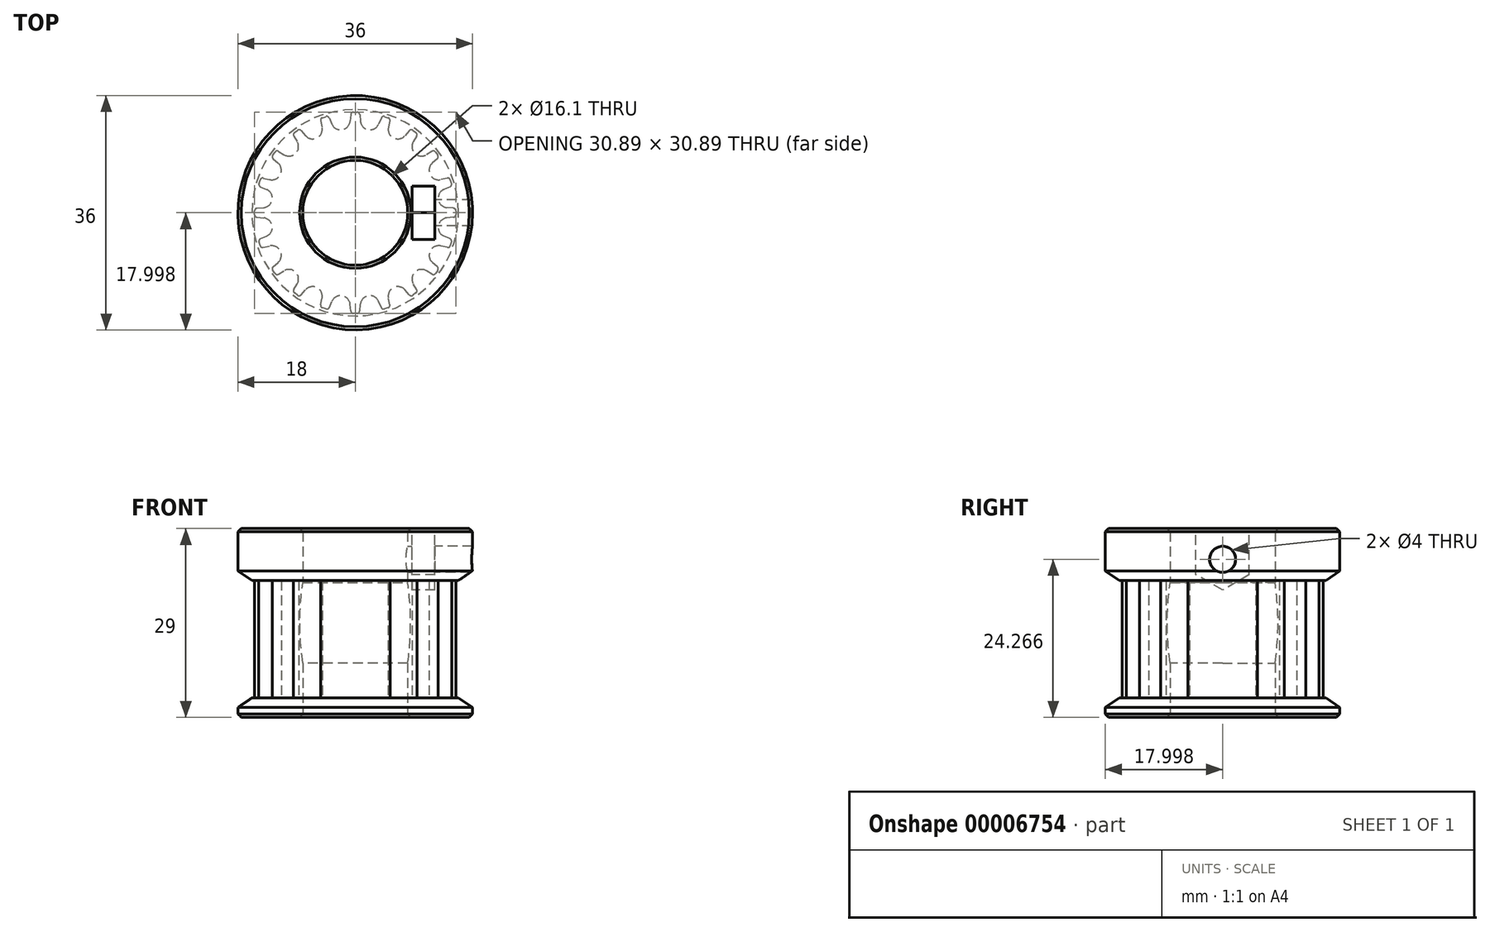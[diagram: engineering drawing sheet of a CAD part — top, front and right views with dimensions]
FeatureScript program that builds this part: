
annotation { "Feature Type Name" : "Feature", "Feature Type Description" : "" }
export const myFeature = defineFeature(function(context is Context, id is Id, definition is map)
    precondition{}
    {
        {
            var Q0;
            Q0=qCreatedBy(makeId("Top.planeOp"),FACE);
            var sketch = newSketch(context, id + "F0", { "sketchPlane" : qUnion([Q0])});
            skLineSegment(sketch, "E0", {"start": v(-0.3, 10.1) * mm, "end": v(0.3, 10.1) * mm});
            skPoint(sketch, "E1", {"position": v(0, 10.1) * mm});
            skArc(sketch, "E2", {"start": v(0.3, 10.1) * mm, "mid": v(0.57, 9.99) * mm, "end": v(0.7, 9.73) * mm});
            skArc(sketch, "E3", {"start": v(-0.3, 10.1) * mm, "mid": v(-0.57, 9.99) * mm, "end": v(-0.7, 9.73) * mm});
            skLineSegment(sketch, "E4", {"start": v(-0.7, 9.73) * mm, "end": v(-0.79, 8.73) * mm});
            skLineSegment(sketch, "E5", {"start": v(0.7, 9.73) * mm, "end": v(0.79, 8.73) * mm});
            skArc(sketch, "E6", {"start": v(-0.79, 8.73) * mm, "mid": v(-2.02, 7.4) * mm, "end": v(-3.6, 8.29) * mm});
            skArc(sketch, "E7.1.0", {"start": v(-5.1, 7.8) * mm, "mid": v(-5.87, 6.16) * mm, "end": v(-7.64, 6.5) * mm});
            skLineSegment(sketch, "E7.1.1", {"start": v(-5.32, 8.77) * mm, "end": v(-5.1, 7.8) * mm});
            skArc(sketch, "E7.1.2", {"start": v(-5.06, 9.25) * mm, "mid": v(-5.28, 9.06) * mm, "end": v(-5.32, 8.77) * mm});
            skLineSegment(sketch, "E7.1.3", {"start": v(-5.06, 9.25) * mm, "end": v(-4.49, 9.43) * mm});
            skArc(sketch, "E7.1.4", {"start": v(-4.49, 9.43) * mm, "mid": v(-4.2, 9.41) * mm, "end": v(-4, 9.2) * mm});
            skLineSegment(sketch, "E7.1.5", {"start": v(-4, 9.2) * mm, "end": v(-3.6, 8.29) * mm});
            skArc(sketch, "E7.2.0", {"start": v(-8.91, 5.58) * mm, "mid": v(-9.14, 3.78) * mm, "end": v(-10.93, 3.56) * mm});
            skLineSegment(sketch, "E7.2.1", {"start": v(-9.43, 6.44) * mm, "end": v(-8.91, 5.58) * mm});
            skArc(sketch, "E7.2.2", {"start": v(-9.32, 6.97) * mm, "mid": v(-9.48, 6.72) * mm, "end": v(-9.43, 6.44) * mm});
            skLineSegment(sketch, "E7.2.3", {"start": v(-9.32, 6.97) * mm, "end": v(-8.84, 7.32) * mm});
            skArc(sketch, "E7.2.4", {"start": v(-8.84, 7.32) * mm, "mid": v(-8.56, 7.4) * mm, "end": v(-8.3, 7.26) * mm});
            skLineSegment(sketch, "E7.2.5", {"start": v(-8.3, 7.26) * mm, "end": v(-7.64, 6.5) * mm});
            skPoint(sketch, "E7.center", {"position": v(0, -5.35) * mm});
            skArc(sketch, "E8.3.3.0", {"start": v(-11.86, 2.3) * mm, "mid": v(-11.51, 0.51) * mm, "end": v(-13.15, -0.25) * mm});
            skLineSegment(sketch, "E8.4.3.0", {"start": v(-12.61, 2.95) * mm, "end": v(-11.86, 2.3) * mm});
            skArc(sketch, "E8.7.3.0", {"start": v(-12.67, 3.48) * mm, "mid": v(-12.75, 3.2) * mm, "end": v(-12.61, 2.95) * mm});
            skLineSegment(sketch, "E8.11.3.0", {"start": v(-12.67, 3.48) * mm, "end": v(-12.32, 3.97) * mm});
            skArc(sketch, "E8.14.3.0", {"start": v(-12.32, 3.97) * mm, "mid": v(-12.08, 4.13) * mm, "end": v(-11.8, 4.08) * mm});
            skLineSegment(sketch, "E8.18.3.0", {"start": v(-11.8, 4.08) * mm, "end": v(-10.93, 3.56) * mm});
            skArc(sketch, "E8.3.4.0", {"start": v(-13.64, -1.75) * mm, "mid": v(-12.76, -3.33) * mm, "end": v(-14.08, -4.57) * mm});
            skLineSegment(sketch, "E8.4.4.0", {"start": v(-14.56, -1.36) * mm, "end": v(-13.64, -1.75) * mm});
            skArc(sketch, "E8.7.4.0", {"start": v(-14.78, -0.86) * mm, "mid": v(-14.77, -1.15) * mm, "end": v(-14.56, -1.36) * mm});
            skLineSegment(sketch, "E8.11.4.0", {"start": v(-14.78, -0.86) * mm, "end": v(-14.6, -0.3) * mm});
            skArc(sketch, "E8.14.4.0", {"start": v(-14.6, -0.3) * mm, "mid": v(-14.41, -0.07) * mm, "end": v(-14.13, -0.03) * mm});
            skLineSegment(sketch, "E8.18.4.0", {"start": v(-14.13, -0.03) * mm, "end": v(-13.15, -0.25) * mm});
            skArc(sketch, "E8.3.5.0", {"start": v(-14.08, -6.14) * mm, "mid": v(-12.76, -7.37) * mm, "end": v(-13.64, -8.96) * mm});
            skLineSegment(sketch, "E8.4.5.0", {"start": v(-15.08, -6.05) * mm, "end": v(-14.08, -6.14) * mm});
            skArc(sketch, "E8.7.5.0", {"start": v(-15.45, -5.65) * mm, "mid": v(-15.34, -5.92) * mm, "end": v(-15.08, -6.05) * mm});
            skLineSegment(sketch, "E8.11.5.0", {"start": v(-15.45, -5.65) * mm, "end": v(-15.45, -5.05) * mm});
            skArc(sketch, "E8.14.5.0", {"start": v(-15.45, -5.05) * mm, "mid": v(-15.34, -4.78) * mm, "end": v(-15.08, -4.65) * mm});
            skLineSegment(sketch, "E8.18.5.0", {"start": v(-15.08, -4.65) * mm, "end": v(-14.08, -4.57) * mm});
            skArc(sketch, "E8.3.6.0", {"start": v(-13.15, -10.45) * mm, "mid": v(-11.51, -11.22) * mm, "end": v(-11.86, -13) * mm});
            skLineSegment(sketch, "E8.4.6.0", {"start": v(-14.13, -10.68) * mm, "end": v(-13.15, -10.45) * mm});
            skArc(sketch, "E8.7.6.0", {"start": v(-14.6, -10.41) * mm, "mid": v(-14.41, -10.63) * mm, "end": v(-14.13, -10.68) * mm});
            skLineSegment(sketch, "E8.11.6.0", {"start": v(-14.6, -10.41) * mm, "end": v(-14.78, -9.84) * mm});
            skArc(sketch, "E8.14.6.0", {"start": v(-14.78, -9.84) * mm, "mid": v(-14.77, -9.55) * mm, "end": v(-14.56, -9.35) * mm});
            skLineSegment(sketch, "E8.18.6.0", {"start": v(-14.56, -9.35) * mm, "end": v(-13.64, -8.96) * mm});
            skArc(sketch, "E8.3.7.0", {"start": v(-10.93, -14.27) * mm, "mid": v(-9.14, -14.49) * mm, "end": v(-8.91, -16.28) * mm});
            skLineSegment(sketch, "E8.4.7.0", {"start": v(-11.8, -14.78) * mm, "end": v(-10.93, -14.27) * mm});
            skArc(sketch, "E8.7.7.0", {"start": v(-12.32, -14.67) * mm, "mid": v(-12.08, -14.83) * mm, "end": v(-11.8, -14.78) * mm});
            skLineSegment(sketch, "E8.11.7.0", {"start": v(-12.32, -14.67) * mm, "end": v(-12.67, -14.19) * mm});
            skArc(sketch, "E8.14.7.0", {"start": v(-12.67, -14.19) * mm, "mid": v(-12.75, -13.9) * mm, "end": v(-12.61, -13.65) * mm});
            skLineSegment(sketch, "E8.18.7.0", {"start": v(-12.61, -13.65) * mm, "end": v(-11.86, -13) * mm});
            skArc(sketch, "E8.3.8.0", {"start": v(-7.64, -17.2) * mm, "mid": v(-5.87, -16.86) * mm, "end": v(-5.1, -18.5) * mm});
            skLineSegment(sketch, "E8.4.8.0", {"start": v(-8.3, -17.96) * mm, "end": v(-7.64, -17.2) * mm});
            skArc(sketch, "E8.7.8.0", {"start": v(-8.84, -18.02) * mm, "mid": v(-8.56, -18.1) * mm, "end": v(-8.3, -17.96) * mm});
            skLineSegment(sketch, "E8.11.8.0", {"start": v(-8.84, -18.02) * mm, "end": v(-9.32, -17.67) * mm});
            skArc(sketch, "E8.14.8.0", {"start": v(-9.32, -17.67) * mm, "mid": v(-9.48, -17.43) * mm, "end": v(-9.43, -17.14) * mm});
            skLineSegment(sketch, "E8.18.8.0", {"start": v(-9.43, -17.14) * mm, "end": v(-8.91, -16.28) * mm});
            skArc(sketch, "E8.3.9.0", {"start": v(-3.6, -18.99) * mm, "mid": v(-2.02, -18.11) * mm, "end": v(-0.79, -19.44) * mm});
            skLineSegment(sketch, "E8.4.9.0", {"start": v(-4, -19.91) * mm, "end": v(-3.6, -18.99) * mm});
            skArc(sketch, "E8.7.9.0", {"start": v(-4.49, -20.13) * mm, "mid": v(-4.2, -20.12) * mm, "end": v(-4, -19.91) * mm});
            skLineSegment(sketch, "E8.11.9.0", {"start": v(-4.49, -20.13) * mm, "end": v(-5.06, -19.95) * mm});
            skArc(sketch, "E8.14.9.0", {"start": v(-5.06, -19.95) * mm, "mid": v(-5.28, -19.77) * mm, "end": v(-5.32, -19.48) * mm});
            skLineSegment(sketch, "E8.18.9.0", {"start": v(-5.32, -19.48) * mm, "end": v(-5.1, -18.5) * mm});
            skArc(sketch, "E8.3.10.0", {"start": v(0.79, -19.44) * mm, "mid": v(2.02, -18.11) * mm, "end": v(3.6, -18.99) * mm});
            skLineSegment(sketch, "E8.4.10.0", {"start": v(0.7, -20.43) * mm, "end": v(0.79, -19.44) * mm});
            skArc(sketch, "E8.7.10.0", {"start": v(0.3, -20.8) * mm, "mid": v(0.57, -20.7) * mm, "end": v(0.7, -20.43) * mm});
            skLineSegment(sketch, "E8.11.10.0", {"start": v(0.3, -20.8) * mm, "end": v(-0.3, -20.8) * mm});
            skArc(sketch, "E8.14.10.0", {"start": v(-0.3, -20.8) * mm, "mid": v(-0.57, -20.7) * mm, "end": v(-0.7, -20.43) * mm});
            skLineSegment(sketch, "E8.18.10.0", {"start": v(-0.7, -20.43) * mm, "end": v(-0.79, -19.44) * mm});
            skArc(sketch, "E8.3.11.0", {"start": v(5.1, -18.5) * mm, "mid": v(5.87, -16.86) * mm, "end": v(7.64, -17.2) * mm});
            skLineSegment(sketch, "E8.4.11.0", {"start": v(5.32, -19.48) * mm, "end": v(5.1, -18.5) * mm});
            skArc(sketch, "E8.7.11.0", {"start": v(5.06, -19.95) * mm, "mid": v(5.28, -19.77) * mm, "end": v(5.32, -19.48) * mm});
            skLineSegment(sketch, "E8.11.11.0", {"start": v(5.06, -19.95) * mm, "end": v(4.49, -20.13) * mm});
            skArc(sketch, "E8.14.11.0", {"start": v(4.49, -20.13) * mm, "mid": v(4.2, -20.12) * mm, "end": v(4, -19.91) * mm});
            skLineSegment(sketch, "E8.18.11.0", {"start": v(4, -19.91) * mm, "end": v(3.6, -18.99) * mm});
            skArc(sketch, "E8.3.12.0", {"start": v(8.91, -16.28) * mm, "mid": v(9.14, -14.49) * mm, "end": v(10.93, -14.27) * mm});
            skLineSegment(sketch, "E8.4.12.0", {"start": v(9.43, -17.14) * mm, "end": v(8.91, -16.28) * mm});
            skArc(sketch, "E8.7.12.0", {"start": v(9.32, -17.67) * mm, "mid": v(9.48, -17.43) * mm, "end": v(9.43, -17.14) * mm});
            skLineSegment(sketch, "E8.11.12.0", {"start": v(9.32, -17.67) * mm, "end": v(8.84, -18.02) * mm});
            skArc(sketch, "E8.14.12.0", {"start": v(8.84, -18.02) * mm, "mid": v(8.56, -18.1) * mm, "end": v(8.3, -17.96) * mm});
            skLineSegment(sketch, "E8.18.12.0", {"start": v(8.3, -17.96) * mm, "end": v(7.64, -17.2) * mm});
            skArc(sketch, "E8.3.13.0", {"start": v(11.86, -13) * mm, "mid": v(11.51, -11.22) * mm, "end": v(13.15, -10.45) * mm});
            skLineSegment(sketch, "E8.4.13.0", {"start": v(12.61, -13.65) * mm, "end": v(11.86, -13) * mm});
            skArc(sketch, "E8.7.13.0", {"start": v(12.67, -14.19) * mm, "mid": v(12.75, -13.9) * mm, "end": v(12.61, -13.65) * mm});
            skLineSegment(sketch, "E8.11.13.0", {"start": v(12.67, -14.19) * mm, "end": v(12.32, -14.67) * mm});
            skArc(sketch, "E8.14.13.0", {"start": v(12.32, -14.67) * mm, "mid": v(12.08, -14.83) * mm, "end": v(11.8, -14.78) * mm});
            skLineSegment(sketch, "E8.18.13.0", {"start": v(11.8, -14.78) * mm, "end": v(10.93, -14.27) * mm});
            skCircle(sketch, "E9", {"center": v(0, -5.35) * mm, "radius": 15.45 * mm, "construction": true});
            skArc(sketch, "E10.3.14.0", {"start": v(13.64, -8.96) * mm, "mid": v(12.76, -7.37) * mm, "end": v(14.08, -6.14) * mm});
            skLineSegment(sketch, "E10.4.14.0", {"start": v(14.56, -9.35) * mm, "end": v(13.64, -8.96) * mm});
            skArc(sketch, "E10.7.14.0", {"start": v(14.78, -9.84) * mm, "mid": v(14.77, -9.55) * mm, "end": v(14.56, -9.35) * mm});
            skLineSegment(sketch, "E10.11.14.0", {"start": v(14.78, -9.84) * mm, "end": v(14.6, -10.41) * mm});
            skArc(sketch, "E10.14.14.0", {"start": v(14.6, -10.41) * mm, "mid": v(14.41, -10.63) * mm, "end": v(14.13, -10.68) * mm});
            skLineSegment(sketch, "E10.18.14.0", {"start": v(14.13, -10.68) * mm, "end": v(13.15, -10.45) * mm});
            skArc(sketch, "E10.3.15.0", {"start": v(14.08, -4.57) * mm, "mid": v(12.76, -3.33) * mm, "end": v(13.64, -1.75) * mm});
            skLineSegment(sketch, "E10.4.15.0", {"start": v(15.08, -4.65) * mm, "end": v(14.08, -4.57) * mm});
            skArc(sketch, "E10.7.15.0", {"start": v(15.45, -5.05) * mm, "mid": v(15.34, -4.78) * mm, "end": v(15.08, -4.65) * mm});
            skLineSegment(sketch, "E10.11.15.0", {"start": v(15.45, -5.05) * mm, "end": v(15.45, -5.65) * mm});
            skArc(sketch, "E10.14.15.0", {"start": v(15.45, -5.65) * mm, "mid": v(15.34, -5.92) * mm, "end": v(15.08, -6.05) * mm});
            skLineSegment(sketch, "E10.18.15.0", {"start": v(15.08, -6.05) * mm, "end": v(14.08, -6.14) * mm});
            skArc(sketch, "E10.3.16.0", {"start": v(13.15, -0.25) * mm, "mid": v(11.51, 0.51) * mm, "end": v(11.86, 2.3) * mm});
            skLineSegment(sketch, "E10.4.16.0", {"start": v(14.13, -0.03) * mm, "end": v(13.15, -0.25) * mm});
            skArc(sketch, "E10.7.16.0", {"start": v(14.6, -0.3) * mm, "mid": v(14.41, -0.07) * mm, "end": v(14.13, -0.03) * mm});
            skLineSegment(sketch, "E10.11.16.0", {"start": v(14.6, -0.3) * mm, "end": v(14.78, -0.86) * mm});
            skArc(sketch, "E10.14.16.0", {"start": v(14.78, -0.86) * mm, "mid": v(14.77, -1.15) * mm, "end": v(14.56, -1.36) * mm});
            skLineSegment(sketch, "E10.18.16.0", {"start": v(14.56, -1.36) * mm, "end": v(13.64, -1.75) * mm});
            skArc(sketch, "E10.3.17.0", {"start": v(10.93, 3.56) * mm, "mid": v(9.14, 3.78) * mm, "end": v(8.91, 5.58) * mm});
            skLineSegment(sketch, "E10.4.17.0", {"start": v(11.8, 4.08) * mm, "end": v(10.93, 3.56) * mm});
            skArc(sketch, "E10.7.17.0", {"start": v(12.32, 3.97) * mm, "mid": v(12.08, 4.13) * mm, "end": v(11.8, 4.08) * mm});
            skLineSegment(sketch, "E10.11.17.0", {"start": v(12.32, 3.97) * mm, "end": v(12.67, 3.48) * mm});
            skArc(sketch, "E10.14.17.0", {"start": v(12.67, 3.48) * mm, "mid": v(12.75, 3.2) * mm, "end": v(12.61, 2.95) * mm});
            skLineSegment(sketch, "E10.18.17.0", {"start": v(12.61, 2.95) * mm, "end": v(11.86, 2.3) * mm});
            skArc(sketch, "E10.3.18.0", {"start": v(7.64, 6.5) * mm, "mid": v(5.87, 6.16) * mm, "end": v(5.1, 7.8) * mm});
            skLineSegment(sketch, "E10.4.18.0", {"start": v(8.3, 7.26) * mm, "end": v(7.64, 6.5) * mm});
            skArc(sketch, "E10.7.18.0", {"start": v(8.84, 7.32) * mm, "mid": v(8.56, 7.4) * mm, "end": v(8.3, 7.26) * mm});
            skLineSegment(sketch, "E10.11.18.0", {"start": v(8.84, 7.32) * mm, "end": v(9.32, 6.97) * mm});
            skArc(sketch, "E10.14.18.0", {"start": v(9.32, 6.97) * mm, "mid": v(9.48, 6.72) * mm, "end": v(9.43, 6.44) * mm});
            skLineSegment(sketch, "E10.18.18.0", {"start": v(9.43, 6.44) * mm, "end": v(8.91, 5.58) * mm});
            skArc(sketch, "E10.3.19.0", {"start": v(3.6, 8.29) * mm, "mid": v(2.02, 7.4) * mm, "end": v(0.79, 8.73) * mm});
            skLineSegment(sketch, "E10.4.19.0", {"start": v(4, 9.2) * mm, "end": v(3.6, 8.29) * mm});
            skArc(sketch, "E10.7.19.0", {"start": v(4.49, 9.43) * mm, "mid": v(4.2, 9.41) * mm, "end": v(4, 9.2) * mm});
            skLineSegment(sketch, "E10.11.19.0", {"start": v(4.49, 9.43) * mm, "end": v(5.06, 9.25) * mm});
            skArc(sketch, "E10.14.19.0", {"start": v(5.06, 9.25) * mm, "mid": v(5.28, 9.06) * mm, "end": v(5.32, 8.77) * mm});
            skLineSegment(sketch, "E10.18.19.0", {"start": v(5.32, 8.77) * mm, "end": v(5.1, 7.8) * mm});
            skCircle(sketch, "E11", {"center": v(0, -5.35) * mm, "radius": 8.05 * mm});
            skSolve(sketch);
        }
        {
            var Q0;
            Q0=makeQuery(id+"F0.imprint","IMPRINT",FACE,{"disambiguationData":[TD([[makeQuery(id+"F0.imprint","IMPRINT",EDGE,{"derivedFrom":sQuery(id+"F0.wireOp",EDGE,"E0")}),-1.0]])]});
            extrude(context, id + "F1", {"entities" : qUnion([Q0]), "endBound" : BoundingType.SYMMETRIC, "depth" : 18 * mm, "offsetDistance" : 25 * mm});
        }
        {
            var Q0;
            Q0=makeQuery(id+"F1.opExtrude","CAP_FACE",FACE,{"disambiguationData":[OSD([sQuery(id+"F0.wireOp",EDGE,"E0"),sQuery(id+"F0.wireOp",EDGE,"E2"),sQuery(id+"F0.wireOp",EDGE,"E3"),sQuery(id+"F0.wireOp",EDGE,"E4"),sQuery(id+"F0.wireOp",EDGE,"E5"),sQuery(id+"F0.wireOp",EDGE,"E6"),sQuery(id+"F0.wireOp",EDGE,"E7.1.0"),sQuery(id+"F0.wireOp",EDGE,"E7.1.1"),sQuery(id+"F0.wireOp",EDGE,"E7.1.2"),sQuery(id+"F0.wireOp",EDGE,"E7.1.3"),sQuery(id+"F0.wireOp",EDGE,"E7.1.4"),sQuery(id+"F0.wireOp",EDGE,"E7.1.5"),sQuery(id+"F0.wireOp",EDGE,"E7.2.0"),sQuery(id+"F0.wireOp",EDGE,"E7.2.1"),sQuery(id+"F0.wireOp",EDGE,"E7.2.2"),sQuery(id+"F0.wireOp",EDGE,"E7.2.3"),sQuery(id+"F0.wireOp",EDGE,"E7.2.4"),sQuery(id+"F0.wireOp",EDGE,"E7.2.5"),sQuery(id+"F0.wireOp",EDGE,"E8.3.3.0"),sQuery(id+"F0.wireOp",EDGE,"E8.4.3.0"),sQuery(id+"F0.wireOp",EDGE,"E8.7.3.0"),sQuery(id+"F0.wireOp",EDGE,"E8.11.3.0"),sQuery(id+"F0.wireOp",EDGE,"E8.14.3.0"),sQuery(id+"F0.wireOp",EDGE,"E8.18.3.0"),sQuery(id+"F0.wireOp",EDGE,"E8.3.4.0"),sQuery(id+"F0.wireOp",EDGE,"E8.4.4.0"),sQuery(id+"F0.wireOp",EDGE,"E8.7.4.0"),sQuery(id+"F0.wireOp",EDGE,"E8.11.4.0"),sQuery(id+"F0.wireOp",EDGE,"E8.14.4.0"),sQuery(id+"F0.wireOp",EDGE,"E8.18.4.0"),sQuery(id+"F0.wireOp",EDGE,"E8.3.5.0"),sQuery(id+"F0.wireOp",EDGE,"E8.4.5.0"),sQuery(id+"F0.wireOp",EDGE,"E8.7.5.0"),sQuery(id+"F0.wireOp",EDGE,"E8.11.5.0"),sQuery(id+"F0.wireOp",EDGE,"E8.14.5.0"),sQuery(id+"F0.wireOp",EDGE,"E8.18.5.0"),sQuery(id+"F0.wireOp",EDGE,"E8.3.6.0"),sQuery(id+"F0.wireOp",EDGE,"E8.4.6.0"),sQuery(id+"F0.wireOp",EDGE,"E8.7.6.0"),sQuery(id+"F0.wireOp",EDGE,"E8.11.6.0"),sQuery(id+"F0.wireOp",EDGE,"E8.14.6.0"),sQuery(id+"F0.wireOp",EDGE,"E8.18.6.0"),sQuery(id+"F0.wireOp",EDGE,"E8.3.7.0"),sQuery(id+"F0.wireOp",EDGE,"E8.4.7.0"),sQuery(id+"F0.wireOp",EDGE,"E8.7.7.0"),sQuery(id+"F0.wireOp",EDGE,"E8.11.7.0"),sQuery(id+"F0.wireOp",EDGE,"E8.14.7.0"),sQuery(id+"F0.wireOp",EDGE,"E8.18.7.0"),sQuery(id+"F0.wireOp",EDGE,"E8.3.8.0"),sQuery(id+"F0.wireOp",EDGE,"E8.4.8.0"),sQuery(id+"F0.wireOp",EDGE,"E8.7.8.0"),sQuery(id+"F0.wireOp",EDGE,"E8.11.8.0"),sQuery(id+"F0.wireOp",EDGE,"E8.14.8.0"),sQuery(id+"F0.wireOp",EDGE,"E8.18.8.0"),sQuery(id+"F0.wireOp",EDGE,"E8.3.9.0"),sQuery(id+"F0.wireOp",EDGE,"E8.4.9.0"),sQuery(id+"F0.wireOp",EDGE,"E8.7.9.0"),sQuery(id+"F0.wireOp",EDGE,"E8.11.9.0"),sQuery(id+"F0.wireOp",EDGE,"E8.14.9.0"),sQuery(id+"F0.wireOp",EDGE,"E8.18.9.0"),sQuery(id+"F0.wireOp",EDGE,"E8.3.10.0"),sQuery(id+"F0.wireOp",EDGE,"E8.4.10.0"),sQuery(id+"F0.wireOp",EDGE,"E8.7.10.0"),sQuery(id+"F0.wireOp",EDGE,"E8.11.10.0"),sQuery(id+"F0.wireOp",EDGE,"E8.14.10.0"),sQuery(id+"F0.wireOp",EDGE,"E8.18.10.0"),sQuery(id+"F0.wireOp",EDGE,"E8.3.11.0"),sQuery(id+"F0.wireOp",EDGE,"E8.4.11.0"),sQuery(id+"F0.wireOp",EDGE,"E8.7.11.0"),sQuery(id+"F0.wireOp",EDGE,"E8.11.11.0"),sQuery(id+"F0.wireOp",EDGE,"E8.14.11.0"),sQuery(id+"F0.wireOp",EDGE,"E8.18.11.0"),sQuery(id+"F0.wireOp",EDGE,"E8.3.12.0"),sQuery(id+"F0.wireOp",EDGE,"E8.4.12.0"),sQuery(id+"F0.wireOp",EDGE,"E8.7.12.0"),sQuery(id+"F0.wireOp",EDGE,"E8.11.12.0"),sQuery(id+"F0.wireOp",EDGE,"E8.14.12.0"),sQuery(id+"F0.wireOp",EDGE,"E8.18.12.0"),sQuery(id+"F0.wireOp",EDGE,"E8.3.13.0"),sQuery(id+"F0.wireOp",EDGE,"E8.4.13.0"),sQuery(id+"F0.wireOp",EDGE,"E8.7.13.0"),sQuery(id+"F0.wireOp",EDGE,"E8.11.13.0"),sQuery(id+"F0.wireOp",EDGE,"E8.14.13.0"),sQuery(id+"F0.wireOp",EDGE,"E8.18.13.0"),sQuery(id+"F0.wireOp",EDGE,"E10.3.14.0"),sQuery(id+"F0.wireOp",EDGE,"E10.4.14.0"),sQuery(id+"F0.wireOp",EDGE,"E10.7.14.0"),sQuery(id+"F0.wireOp",EDGE,"E10.11.14.0"),sQuery(id+"F0.wireOp",EDGE,"E10.14.14.0"),sQuery(id+"F0.wireOp",EDGE,"E10.18.14.0"),sQuery(id+"F0.wireOp",EDGE,"E10.3.15.0"),sQuery(id+"F0.wireOp",EDGE,"E10.4.15.0"),sQuery(id+"F0.wireOp",EDGE,"E10.7.15.0"),sQuery(id+"F0.wireOp",EDGE,"E10.11.15.0"),sQuery(id+"F0.wireOp",EDGE,"E10.14.15.0"),sQuery(id+"F0.wireOp",EDGE,"E10.18.15.0"),sQuery(id+"F0.wireOp",EDGE,"E10.3.16.0"),sQuery(id+"F0.wireOp",EDGE,"E10.4.16.0"),sQuery(id+"F0.wireOp",EDGE,"E10.7.16.0"),sQuery(id+"F0.wireOp",EDGE,"E10.11.16.0"),sQuery(id+"F0.wireOp",EDGE,"E10.14.16.0"),sQuery(id+"F0.wireOp",EDGE,"E10.18.16.0"),sQuery(id+"F0.wireOp",EDGE,"E10.3.17.0"),sQuery(id+"F0.wireOp",EDGE,"E10.4.17.0"),sQuery(id+"F0.wireOp",EDGE,"E10.7.17.0"),sQuery(id+"F0.wireOp",EDGE,"E10.11.17.0"),sQuery(id+"F0.wireOp",EDGE,"E10.14.17.0"),sQuery(id+"F0.wireOp",EDGE,"E10.18.17.0"),sQuery(id+"F0.wireOp",EDGE,"E10.3.18.0"),sQuery(id+"F0.wireOp",EDGE,"E10.4.18.0"),sQuery(id+"F0.wireOp",EDGE,"E10.7.18.0"),sQuery(id+"F0.wireOp",EDGE,"E10.11.18.0"),sQuery(id+"F0.wireOp",EDGE,"E10.14.18.0"),sQuery(id+"F0.wireOp",EDGE,"E10.18.18.0"),sQuery(id+"F0.wireOp",EDGE,"E10.3.19.0"),sQuery(id+"F0.wireOp",EDGE,"E10.4.19.0"),sQuery(id+"F0.wireOp",EDGE,"E10.7.19.0"),sQuery(id+"F0.wireOp",EDGE,"E10.11.19.0"),sQuery(id+"F0.wireOp",EDGE,"E10.14.19.0"),sQuery(id+"F0.wireOp",EDGE,"E10.18.19.0")])],"isStart":false});
            var sketch = newSketch(context, id + "F2", { "sketchPlane" : qUnion([Q0])});
            skCircle(sketch, "E12", {"center": v(0, -5.35) * mm, "radius": 18 * mm});
            skSolve(sketch);
        }
        {
            var Q0;
            Q0=makeQuery(id+"F2.imprint","IMPRINT",FACE,{"disambiguationData":[TD([[makeQuery(id+"F2.imprint","IMPRINT",EDGE,{"derivedFrom":makeQuery(id+"F1.opExtrude","CAP_EDGE",EDGE,{"disambiguationData":[OSD([sQuery(id+"F0.wireOp",EDGE,"E0")])],"isStart":false})}),-1.0]])]});
            var Q1;
            Q1=makeQuery(id+"F2.imprint","IMPRINT",FACE,{"disambiguationData":[TD([[makeQuery(id+"F2.imprint","IMPRINT",EDGE,{"derivedFrom":sQuery(id+"F2.wireOp",EDGE,"E12")}),1.0]])]});
            extrude(context, id + "F3", {"entities" : qUnion([Q0, Q1]), "operationType" : NewBodyOperationType.ADD, "depth" : 8 * mm, "offsetDistance" : 25 * mm});
        }
        {
            var Q0;
            Q0=makeQuery(id+"F1.opExtrude","CAP_FACE",FACE,{"disambiguationData":[OSD([sQuery(id+"F0.wireOp",EDGE,"E0"),sQuery(id+"F0.wireOp",EDGE,"E2"),sQuery(id+"F0.wireOp",EDGE,"E3"),sQuery(id+"F0.wireOp",EDGE,"E4"),sQuery(id+"F0.wireOp",EDGE,"E5"),sQuery(id+"F0.wireOp",EDGE,"E6"),sQuery(id+"F0.wireOp",EDGE,"E7.1.0"),sQuery(id+"F0.wireOp",EDGE,"E7.1.1"),sQuery(id+"F0.wireOp",EDGE,"E7.1.2"),sQuery(id+"F0.wireOp",EDGE,"E7.1.3"),sQuery(id+"F0.wireOp",EDGE,"E7.1.4"),sQuery(id+"F0.wireOp",EDGE,"E7.1.5"),sQuery(id+"F0.wireOp",EDGE,"E7.2.0"),sQuery(id+"F0.wireOp",EDGE,"E7.2.1"),sQuery(id+"F0.wireOp",EDGE,"E7.2.2"),sQuery(id+"F0.wireOp",EDGE,"E7.2.3"),sQuery(id+"F0.wireOp",EDGE,"E7.2.4"),sQuery(id+"F0.wireOp",EDGE,"E7.2.5"),sQuery(id+"F0.wireOp",EDGE,"E8.3.3.0"),sQuery(id+"F0.wireOp",EDGE,"E8.4.3.0"),sQuery(id+"F0.wireOp",EDGE,"E8.7.3.0"),sQuery(id+"F0.wireOp",EDGE,"E8.11.3.0"),sQuery(id+"F0.wireOp",EDGE,"E8.14.3.0"),sQuery(id+"F0.wireOp",EDGE,"E8.18.3.0"),sQuery(id+"F0.wireOp",EDGE,"E8.3.4.0"),sQuery(id+"F0.wireOp",EDGE,"E8.4.4.0"),sQuery(id+"F0.wireOp",EDGE,"E8.7.4.0"),sQuery(id+"F0.wireOp",EDGE,"E8.11.4.0"),sQuery(id+"F0.wireOp",EDGE,"E8.14.4.0"),sQuery(id+"F0.wireOp",EDGE,"E8.18.4.0"),sQuery(id+"F0.wireOp",EDGE,"E8.3.5.0"),sQuery(id+"F0.wireOp",EDGE,"E8.4.5.0"),sQuery(id+"F0.wireOp",EDGE,"E8.7.5.0"),sQuery(id+"F0.wireOp",EDGE,"E8.11.5.0"),sQuery(id+"F0.wireOp",EDGE,"E8.14.5.0"),sQuery(id+"F0.wireOp",EDGE,"E8.18.5.0"),sQuery(id+"F0.wireOp",EDGE,"E8.3.6.0"),sQuery(id+"F0.wireOp",EDGE,"E8.4.6.0"),sQuery(id+"F0.wireOp",EDGE,"E8.7.6.0"),sQuery(id+"F0.wireOp",EDGE,"E8.11.6.0"),sQuery(id+"F0.wireOp",EDGE,"E8.14.6.0"),sQuery(id+"F0.wireOp",EDGE,"E8.18.6.0"),sQuery(id+"F0.wireOp",EDGE,"E8.3.7.0"),sQuery(id+"F0.wireOp",EDGE,"E8.4.7.0"),sQuery(id+"F0.wireOp",EDGE,"E8.7.7.0"),sQuery(id+"F0.wireOp",EDGE,"E8.11.7.0"),sQuery(id+"F0.wireOp",EDGE,"E8.14.7.0"),sQuery(id+"F0.wireOp",EDGE,"E8.18.7.0"),sQuery(id+"F0.wireOp",EDGE,"E8.3.8.0"),sQuery(id+"F0.wireOp",EDGE,"E8.4.8.0"),sQuery(id+"F0.wireOp",EDGE,"E8.7.8.0"),sQuery(id+"F0.wireOp",EDGE,"E8.11.8.0"),sQuery(id+"F0.wireOp",EDGE,"E8.14.8.0"),sQuery(id+"F0.wireOp",EDGE,"E8.18.8.0"),sQuery(id+"F0.wireOp",EDGE,"E8.3.9.0"),sQuery(id+"F0.wireOp",EDGE,"E8.4.9.0"),sQuery(id+"F0.wireOp",EDGE,"E8.7.9.0"),sQuery(id+"F0.wireOp",EDGE,"E8.11.9.0"),sQuery(id+"F0.wireOp",EDGE,"E8.14.9.0"),sQuery(id+"F0.wireOp",EDGE,"E8.18.9.0"),sQuery(id+"F0.wireOp",EDGE,"E8.3.10.0"),sQuery(id+"F0.wireOp",EDGE,"E8.4.10.0"),sQuery(id+"F0.wireOp",EDGE,"E8.7.10.0"),sQuery(id+"F0.wireOp",EDGE,"E8.11.10.0"),sQuery(id+"F0.wireOp",EDGE,"E8.14.10.0"),sQuery(id+"F0.wireOp",EDGE,"E8.18.10.0"),sQuery(id+"F0.wireOp",EDGE,"E8.3.11.0"),sQuery(id+"F0.wireOp",EDGE,"E8.4.11.0"),sQuery(id+"F0.wireOp",EDGE,"E8.7.11.0"),sQuery(id+"F0.wireOp",EDGE,"E8.11.11.0"),sQuery(id+"F0.wireOp",EDGE,"E8.14.11.0"),sQuery(id+"F0.wireOp",EDGE,"E8.18.11.0"),sQuery(id+"F0.wireOp",EDGE,"E8.3.12.0"),sQuery(id+"F0.wireOp",EDGE,"E8.4.12.0"),sQuery(id+"F0.wireOp",EDGE,"E8.7.12.0"),sQuery(id+"F0.wireOp",EDGE,"E8.11.12.0"),sQuery(id+"F0.wireOp",EDGE,"E8.14.12.0"),sQuery(id+"F0.wireOp",EDGE,"E8.18.12.0"),sQuery(id+"F0.wireOp",EDGE,"E8.3.13.0"),sQuery(id+"F0.wireOp",EDGE,"E8.4.13.0"),sQuery(id+"F0.wireOp",EDGE,"E8.7.13.0"),sQuery(id+"F0.wireOp",EDGE,"E8.11.13.0"),sQuery(id+"F0.wireOp",EDGE,"E8.14.13.0"),sQuery(id+"F0.wireOp",EDGE,"E8.18.13.0"),sQuery(id+"F0.wireOp",EDGE,"E10.3.14.0"),sQuery(id+"F0.wireOp",EDGE,"E10.4.14.0"),sQuery(id+"F0.wireOp",EDGE,"E10.7.14.0"),sQuery(id+"F0.wireOp",EDGE,"E10.11.14.0"),sQuery(id+"F0.wireOp",EDGE,"E10.14.14.0"),sQuery(id+"F0.wireOp",EDGE,"E10.18.14.0"),sQuery(id+"F0.wireOp",EDGE,"E10.3.15.0"),sQuery(id+"F0.wireOp",EDGE,"E10.4.15.0"),sQuery(id+"F0.wireOp",EDGE,"E10.7.15.0"),sQuery(id+"F0.wireOp",EDGE,"E10.11.15.0"),sQuery(id+"F0.wireOp",EDGE,"E10.14.15.0"),sQuery(id+"F0.wireOp",EDGE,"E10.18.15.0"),sQuery(id+"F0.wireOp",EDGE,"E10.3.16.0"),sQuery(id+"F0.wireOp",EDGE,"E10.4.16.0"),sQuery(id+"F0.wireOp",EDGE,"E10.7.16.0"),sQuery(id+"F0.wireOp",EDGE,"E10.11.16.0"),sQuery(id+"F0.wireOp",EDGE,"E10.14.16.0"),sQuery(id+"F0.wireOp",EDGE,"E10.18.16.0"),sQuery(id+"F0.wireOp",EDGE,"E10.3.17.0"),sQuery(id+"F0.wireOp",EDGE,"E10.4.17.0"),sQuery(id+"F0.wireOp",EDGE,"E10.7.17.0"),sQuery(id+"F0.wireOp",EDGE,"E10.11.17.0"),sQuery(id+"F0.wireOp",EDGE,"E10.14.17.0"),sQuery(id+"F0.wireOp",EDGE,"E10.18.17.0"),sQuery(id+"F0.wireOp",EDGE,"E10.3.18.0"),sQuery(id+"F0.wireOp",EDGE,"E10.4.18.0"),sQuery(id+"F0.wireOp",EDGE,"E10.7.18.0"),sQuery(id+"F0.wireOp",EDGE,"E10.11.18.0"),sQuery(id+"F0.wireOp",EDGE,"E10.14.18.0"),sQuery(id+"F0.wireOp",EDGE,"E10.18.18.0"),sQuery(id+"F0.wireOp",EDGE,"E10.3.19.0"),sQuery(id+"F0.wireOp",EDGE,"E10.4.19.0"),sQuery(id+"F0.wireOp",EDGE,"E10.7.19.0"),sQuery(id+"F0.wireOp",EDGE,"E10.11.19.0"),sQuery(id+"F0.wireOp",EDGE,"E10.14.19.0"),sQuery(id+"F0.wireOp",EDGE,"E10.18.19.0"),sQuery(id+"F0.wireOp",EDGE,"E11")])],"isStart":true});
            var sketch = newSketch(context, id + "F4", { "sketchPlane" : qUnion([Q0])});
            skCircle(sketch, "E13", {"center": v(0, 5.35) * mm, "radius": 18 * mm});
            skSolve(sketch);
        }
        {
            var Q0;
            Q0=makeQuery(id+"F4.imprint","IMPRINT",FACE,{"disambiguationData":[TD([[makeQuery(id+"F4.imprint","IMPRINT",EDGE,{"derivedFrom":makeQuery(id+"F1.opExtrude","CAP_EDGE",EDGE,{"disambiguationData":[OSD([sQuery(id+"F0.wireOp",EDGE,"E0")])],"isStart":true})}),1.0]])]});
            var Q1;
            Q1=makeQuery(id+"F4.imprint","IMPRINT",FACE,{"disambiguationData":[TD([[makeQuery(id+"F4.imprint","IMPRINT",EDGE,{"derivedFrom":sQuery(id+"F4.wireOp",EDGE,"E13")}),1.0]])]});
            extrude(context, id + "F5", {"entities" : qUnion([Q0, Q1]), "operationType" : NewBodyOperationType.ADD, "depth" : 3 * mm, "offsetDistance" : 25 * mm});
        }
        {
            var Q0;
            Q0=makeQuery(id+"F3.opExtrude","CAP_EDGE",EDGE,{"disambiguationData":[OSD([sQuery(id+"F2.wireOp",EDGE,"E12")])],"isStart":true});
            var Q1;
            Q1=makeQuery(id+"F5.opExtrude","CAP_EDGE",EDGE,{"disambiguationData":[OSD([sQuery(id+"F4.wireOp",EDGE,"E13")])],"isStart":true});
            chamfer(context, id + "F6", {"entities" : qUnion([Q0, Q1]), "chamferType" : ChamferType.OFFSET_ANGLE, "width" : 1.5 * mm, "oppositeDirection" : false, "angle" : 55 * degree, "tangentPropagation" : true});
        }
        {
            var Q0;
            Q0=qCreatedBy(makeId("Right.planeOp"),FACE);
            cPlane(context, id + "F7", {"entities" : qUnion([Q0]), "cplaneType" : CPlaneType.OFFSET, "offset" : 10.5 * mm, "width" : 150 * mm, "height" : 150 * mm});
        }
        {
            var Q0;
            Q0=qCreatedBy(id+"F7.planeOp",FACE);
            var sketch = newSketch(context, id + "F8", { "sketchPlane" : qUnion([Q0])});
            skLineSegment(sketch, "E14.0", {"start": v(-13.4, 17) * mm, "end": v(2.7, 17) * mm});
            skLineSegment(sketch, "E15", {"start": v(-9.45, 17) * mm, "end": v(-9.45, 14.63) * mm});
            skLineSegment(sketch, "E16", {"start": v(-1.25, 14.63) * mm, "end": v(-1.25, 17) * mm});
            skPoint(sketch, "E17", {"position": v(-5.35, 17) * mm});
            skCircle(sketch, "E18.cCircle", {"center": v(-5.35, 12.27) * mm, "radius": 4.1 * mm, "construction": true});
            skLineSegment(sketch, "E18.0", {"start": v(-9.45, 9.9) * mm, "end": v(-9.45, 14.63) * mm});
            skLineSegment(sketch, "E18.1", {"start": v(-9.45, 14.63) * mm, "end": v(-5.35, 17) * mm});
            skLineSegment(sketch, "E18.2", {"start": v(-5.35, 17) * mm, "end": v(-1.25, 14.63) * mm});
            skLineSegment(sketch, "E18.3", {"start": v(-1.25, 14.63) * mm, "end": v(-1.25, 9.9) * mm});
            skLineSegment(sketch, "E18.4", {"start": v(-1.25, 9.9) * mm, "end": v(-5.35, 7.53) * mm});
            skLineSegment(sketch, "E18.5", {"start": v(-5.35, 7.53) * mm, "end": v(-9.45, 9.9) * mm});
            skPoint(sketch, "E18.0.midPoint", {"position": v(-9.45, 12.27) * mm});
            skCircle(sketch, "E19", {"center": v(-5.35, 12.27) * mm, "radius": 2 * mm});
            skSolve(sketch);
        }
        {
            var Q0;
            {var subQ0=sQuery(id+"F8.wireOp",EDGE,"E16");Q0=makeQuery(id+"F8.imprint","IMPRINT",FACE,{"disambiguationData":[TD([[makeQuery(id+"F8.imprint","IMPRINT",EDGE,{"derivedFrom":subQ0}),1.0]])]});}
            var Q1;
            Q1=makeQuery(id+"F8.imprint","IMPRINT",FACE,{"disambiguationData":[TD([[makeQuery(id+"F8.imprint","IMPRINT",EDGE,{"derivedFrom":sQuery(id+"F8.wireOp",EDGE,"E18.0")}),-1.0]])]});
            var Q2;
            Q2=makeQuery(id+"F8.imprint","IMPRINT",FACE,{"disambiguationData":[TD([[makeQuery(id+"F8.imprint","IMPRINT",EDGE,{"derivedFrom":sQuery(id+"F8.wireOp",EDGE,"E19")}),1.0]])]});
            var Q3;
            {var subQ0=sQuery(id+"F8.wireOp",EDGE,"E15");Q3=makeQuery(id+"F8.imprint","IMPRINT",FACE,{"disambiguationData":[TD([[makeQuery(id+"F8.imprint","IMPRINT",EDGE,{"derivedFrom":subQ0}),1.0]])]});}
            extrude(context, id + "F9", {"entities" : qUnion([Q0, Q1, Q2, Q3]), "operationType" : NewBodyOperationType.REMOVE, "endBound" : BoundingType.SYMMETRIC, "depth" : 3.5 * mm, "offsetDistance" : 25 * mm});
        }
        {
            var Q0;
            Q0=makeQuery(id+"F8.imprint","IMPRINT",FACE,{"disambiguationData":[TD([[makeQuery(id+"F8.imprint","IMPRINT",EDGE,{"derivedFrom":sQuery(id+"F8.wireOp",EDGE,"E19")}),1.0]])]});
            var Q1;
            {var subQ0=sQuery(id+"F0.wireOp",EDGE,"E11");Q1=makeQuery(id+"F3.boolean.opBoolean","MERGE",FACE,{"derivedFrom":[makeQuery(id+"F1.opExtrude","SWEPT_FACE",FACE,{"disambiguationData":[OSD([subQ0])]}),makeQuery(id+"F3.opExtrude","SWEPT_FACE",FACE,{"disambiguationData":[OSD([subQ0])]})]});}
            extrude(context, id + "F10", {"entities" : qUnion([Q0]), "operationType" : NewBodyOperationType.REMOVE, "endBound" : BoundingType.THROUGH_ALL, "depth" : 25 * mm, "endBoundEntityFace" : qUnion([Q1]), "offsetDistance" : 25 * mm});
        }
        {
            var Q0;
            Q0=makeQuery(id+"F8.imprint","IMPRINT",FACE,{"disambiguationData":[TD([[makeQuery(id+"F8.imprint","IMPRINT",EDGE,{"derivedFrom":sQuery(id+"F8.wireOp",EDGE,"E19")}),1.0]])]});
            var Q1;
            {var subQ0=sQuery(id+"F0.wireOp",EDGE,"E11");Q1=makeQuery(id+"F5.boolean.opBoolean","MERGE",FACE,{"derivedFrom":[makeQuery(id+"F3.boolean.opBoolean","MERGE",FACE,{"derivedFrom":[makeQuery(id+"F1.opExtrude","SWEPT_FACE",FACE,{"disambiguationData":[OSD([subQ0])]}),makeQuery(id+"F3.opExtrude","SWEPT_FACE",FACE,{"disambiguationData":[OSD([subQ0])]})]}),makeQuery(id+"F5.opExtrude","SWEPT_FACE",FACE,{"disambiguationData":[OSD([subQ0])]})]});}
            extrude(context, id + "F11", {"entities" : qUnion([Q0]), "operationType" : NewBodyOperationType.REMOVE, "endBound" : BoundingType.UP_TO_SURFACE, "oppositeDirection" : true, "depth" : 25 * mm, "endBoundEntityFace" : qUnion([Q1]), "offsetDistance" : 25 * mm});
        }
        {
            var Q0;
            Q0=makeQuery(id+"F5.opExtrude","CAP_EDGE",EDGE,{"disambiguationData":[OSD([sQuery(id+"F0.wireOp",EDGE,"E11")])],"isStart":false});
            var Q1;
            Q1=makeQuery(id+"F3.opExtrude","CAP_EDGE",EDGE,{"disambiguationData":[OSD([sQuery(id+"F0.wireOp",EDGE,"E11")])],"isStart":false});
            var Q2;
            Q2=makeQuery(id+"F3.opExtrude","CAP_EDGE",EDGE,{"disambiguationData":[OSD([sQuery(id+"F2.wireOp",EDGE,"E12")])],"isStart":false});
            var Q3;
            Q3=makeQuery(id+"F5.opExtrude","CAP_EDGE",EDGE,{"disambiguationData":[OSD([sQuery(id+"F4.wireOp",EDGE,"E13")])],"isStart":false});
            var Q4;
            Q4=makeQuery(id+"F9.boolean.opBoolean","COPY",EDGE,{"derivedFrom":makeQuery(id+"F9.opExtrude","CAP_EDGE",EDGE,{"disambiguationData":[OSD([sQuery(id+"F8.wireOp",EDGE,"E14.0")])],"isStart":true})});
            var Q5;
            Q5=makeQuery(id+"F9.boolean.opBoolean","COPY",EDGE,{"derivedFrom":makeQuery(id+"F9.opExtrude","SWEPT_EDGE",EDGE,{"disambiguationData":[OSD([sQuery(id+"F8.wireOp",EDGE,"E14.0"),sQuery(id+"F8.wireOp",EDGE,"E15")])]})});
            var Q6;
            Q6=makeQuery(id+"F9.boolean.opBoolean","COPY",EDGE,{"derivedFrom":makeQuery(id+"F9.opExtrude","CAP_EDGE",EDGE,{"disambiguationData":[OSD([sQuery(id+"F8.wireOp",EDGE,"E14.0")])],"isStart":false})});
            var Q7;
            Q7=makeQuery(id+"F9.boolean.opBoolean","COPY",EDGE,{"derivedFrom":makeQuery(id+"F9.opExtrude","SWEPT_EDGE",EDGE,{"disambiguationData":[OSD([sQuery(id+"F8.wireOp",EDGE,"E14.0"),sQuery(id+"F8.wireOp",EDGE,"E16")])]})});
            chamfer(context, id + "F12", {"entities" : qUnion([Q0, Q1, Q2, Q3, Q4, Q5, Q6, Q7]), "width" : .5 * mm, "tangentPropagation" : true});
        }
        {
            var Q0;
            Q0=qCreatedBy(makeId("Right.planeOp"),FACE);
            var sketch = newSketch(context, id + "F13", { "sketchPlane" : qUnion([Q0])});
            skLineSegment(sketch, "E20.0", {"start": v(3.2, 17) * mm, "end": v(-13.9, 17) * mm});
            skLineSegment(sketch, "E20.1", {"start": v(-13.9, -12) * mm, "end": v(3.2, -12) * mm});
            skLineSegment(sketch, "E21", {"start": v(-13.35, 17) * mm, "end": v(-13.35, 9) * mm});
            skLineSegment(sketch, "E22", {"start": v(-13.35, 9) * mm, "end": v(-13.35, -4) * mm});
            skLineSegment(sketch, "E23", {"start": v(-13.35, -4) * mm, "end": v(-13.35, -12) * mm});
            skArc(sketch, "E24", {"start": v(-13.35, 9) * mm, "mid": v(-13.85, 2.5) * mm, "end": v(-13.35, -4) * mm});
            skPoint(sketch, "E25", {"position": v(-5.35, 17) * mm});
            skLineSegment(sketch, "E26", {"start": v(-5.35, 17) * mm, "end": v(-5.35, 6.76) * mm, "construction": true});
            skSolve(sketch);
        }
        {
            var Q0;
            Q0=makeQuery(id+"F13.imprint","IMPRINT",FACE,{"disambiguationData":[TD([[makeQuery(id+"F13.imprint","IMPRINT",EDGE,{"derivedFrom":sQuery(id+"F13.wireOp",EDGE,"E22")}),-1.0]])]});
            var Q1;
            Q1=sQuery(id+"F13.wireOp",EDGE,"E26");
            revolve(context, id + "F14", {"operationType" : NewBodyOperationType.REMOVE, "entities" : qUnion([Q0]), "axis" : qUnion([Q1]), "revolveType" : RevolveType.FULL, "oppositeDirection" : true});
        }
    });
